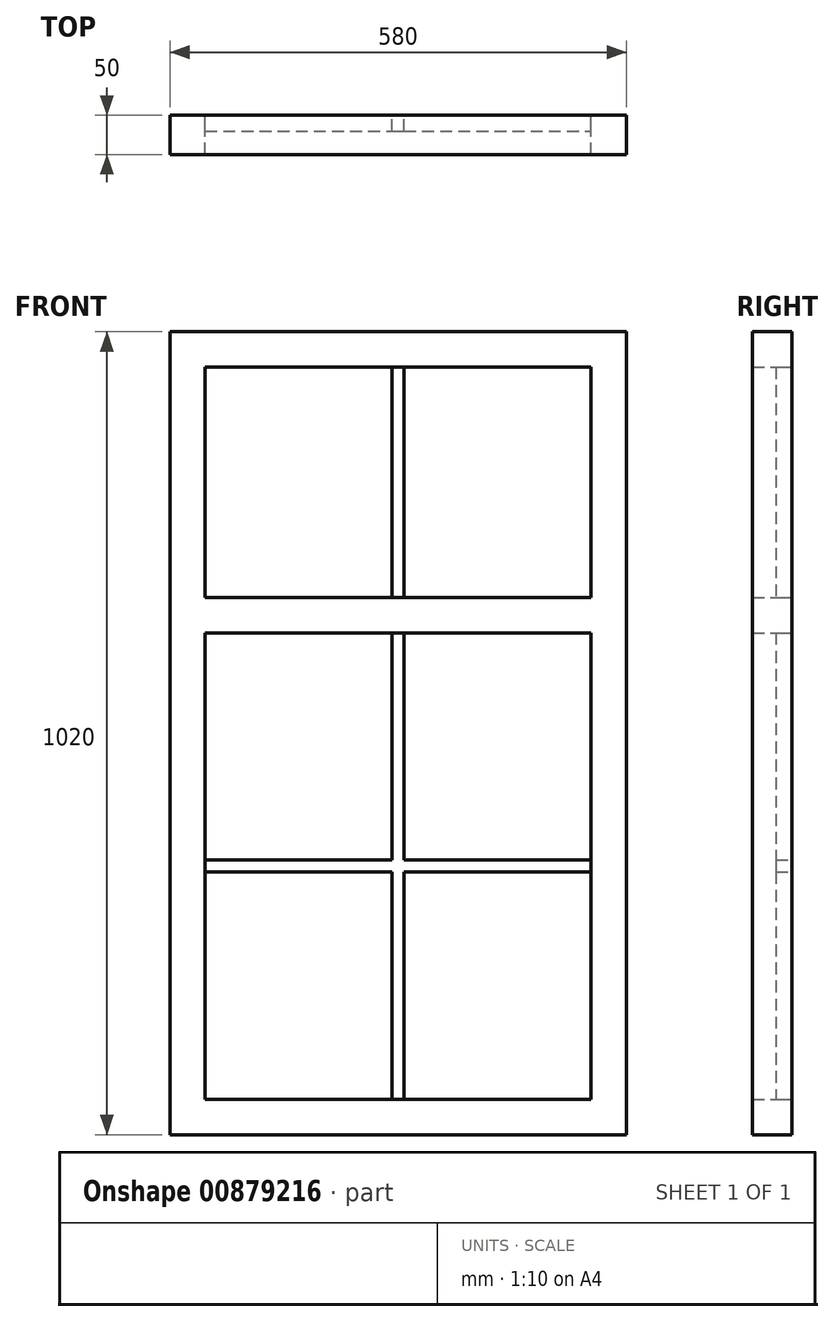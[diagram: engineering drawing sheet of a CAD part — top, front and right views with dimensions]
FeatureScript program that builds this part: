
annotation { "Feature Type Name" : "Feature", "Feature Type Description" : "" }
export const myFeature = defineFeature(function(context is Context, id is Id, definition is map)
    precondition{}
    {
        {
            var Q0;
            Q0=qCreatedBy(makeId("Front.planeOp"),FACE);
            var sketch = newSketch(context, id + "F0", { "sketchPlane" : qUnion([Q0])});
            skLineSegment(sketch, "E0.bottom", {"start": v(0, 0) * mm, "end": v(580, 0) * mm});
            skLineSegment(sketch, "E0.top", {"start": v(0, 1020) * mm, "end": v(580, 1020) * mm});
            skLineSegment(sketch, "E0.left", {"start": v(0, 0) * mm, "end": v(0, 1020) * mm});
            skLineSegment(sketch, "E0.right", {"start": v(580, 0) * mm, "end": v(580, 1020) * mm});
            skLineSegment(sketch, "E1.bottom", {"start": v(45, 975) * mm, "end": v(535, 975) * mm});
            skLineSegment(sketch, "E1.top", {"start": v(45, 45) * mm, "end": v(535, 45) * mm});
            skLineSegment(sketch, "E1.left", {"start": v(45, 975) * mm, "end": v(45, 682.5) * mm});
            skLineSegment(sketch, "E1.right", {"start": v(535, 975) * mm, "end": v(535, 682.5) * mm});
            skLineSegment(sketch, "E2.bottom", {"start": v(45, 682.5) * mm, "end": v(535, 682.5) * mm});
            skLineSegment(sketch, "E2.top", {"start": v(45, 637.5) * mm, "end": v(535, 637.5) * mm});
            skLineSegment(sketch, "E3.trimOffspring", {"start": v(535, 637.5) * mm, "end": v(535, 45) * mm});
            skLineSegment(sketch, "E4.trimOffspring", {"start": v(45, 637.5) * mm, "end": v(45, 45) * mm});
            skSolve(sketch);
        }
        {
            var Q0;
            Q0=qSketchRegion(id+"F0",true);
            extrude(context, id + "F1", {"entities" : qUnion([Q0]), "depth" : 50 * mm, "offsetDistance" : 25 * mm});
        }
        {
            var Q0;
            Q0=qCreatedBy(makeId("Front.planeOp"),FACE);
            var sketch = newSketch(context, id + "F2", { "sketchPlane" : qUnion([Q0])});
            skLineSegment(sketch, "E5.bottom", {"start": v(282.5, 975) * mm, "end": v(297.5, 975) * mm});
            skLineSegment(sketch, "E5.top", {"start": v(282.5, 682.5) * mm, "end": v(297.5, 682.5) * mm});
            skLineSegment(sketch, "E5.left", {"start": v(282.5, 975) * mm, "end": v(282.5, 682.5) * mm});
            skLineSegment(sketch, "E5.right", {"start": v(297.5, 975) * mm, "end": v(297.5, 682.5) * mm});
            skLineSegment(sketch, "E6.bottom", {"start": v(282.5, 637.5) * mm, "end": v(297.5, 637.5) * mm});
            skLineSegment(sketch, "E6.top", {"start": v(282.5, 45) * mm, "end": v(297.5, 45) * mm});
            skLineSegment(sketch, "E6.left", {"start": v(282.5, 637.5) * mm, "end": v(282.5, 348.75) * mm});
            skLineSegment(sketch, "E6.right", {"start": v(297.5, 637.5) * mm, "end": v(297.5, 348.75) * mm});
            skLineSegment(sketch, "E7.bottom", {"start": v(45, 348.75) * mm, "end": v(282.5, 348.75) * mm});
            skLineSegment(sketch, "E7.top", {"start": v(45, 333.75) * mm, "end": v(282.5, 333.75) * mm});
            skLineSegment(sketch, "E7.left", {"start": v(45, 348.75) * mm, "end": v(45, 333.75) * mm});
            skLineSegment(sketch, "E7.right", {"start": v(535, 348.75) * mm, "end": v(535, 333.75) * mm});
            skLineSegment(sketch, "E8.trimOffspring", {"start": v(297.5, 348.75) * mm, "end": v(535, 348.75) * mm});
            skLineSegment(sketch, "E9.trimOffspring", {"start": v(282.5, 333.75) * mm, "end": v(282.5, 45) * mm});
            skLineSegment(sketch, "E10.trimOffspring", {"start": v(297.5, 333.75) * mm, "end": v(535, 333.75) * mm});
            skLineSegment(sketch, "E11.trimOffspring", {"start": v(297.5, 333.75) * mm, "end": v(297.5, 45) * mm});
            skSolve(sketch);
        }
        {
            var Q0;
            Q0=qSketchRegion(id+"F2",true);
            extrude(context, id + "F3", {"entities" : qUnion([Q0]), "operationType" : NewBodyOperationType.ADD, "depth" : 20 * mm, "offsetDistance" : 25 * mm});
        }
    });
